# Revit family: IS_CerathermNavigo_A7295_BIM_NL
name_source: partatom
category: Plumbing Fixtures
units: mm (PartAtom-declared; Revit-internal decimal feet)

## family parameters
Always vertical = No
Cut with Voids When Loaded = No
OmniClass Number = 23.45.55.17
OmniClass Title = Mixing Faucets
Part Type = Normal
Room Calculation Point = No
Round Connector Dimension = Use Diameter
Shared = No
Work Plane-Based = No

## types (4) — shared parameters
Accesoires = https://www.idealstandard.nl
Accessories = https://www.idealstandard.nl
Afmetingen = 157 x 44 x 157 mm
AfstandsEenheid = Millimeter
AreaUnits = millimeter
Artikelreferentie = Ceratherm Navigo Thermal Shower 1-Control
AssetType = Shower Mixer
Auteur = Ideal Standard
BIMObjectName = IS_IdealStandard_ShowerMixers_CerathermNavigo_A7295
BIMobject category = Taps & Mixers
BIMobject category code = sanitary-taps-mixers
BIMobject main category = Sanitary
BIMobject main category code = sanitary
Beschrijvinggarantie = Herstellergarantie
BimObjectNaam = IS_IdealStandard_ShowerMixers_CerathermNavigo_A7295
Brand = Ideal Standard
Brand url = https://www.idealstandard.nl
Breedte = 157.100021
ConnectionType = Plumbing
CurrencyUnit = €
CurrentRevision = 1
Date of publishing = 01/04/2022
Diepte = 44 mm
Douchebak = No
DurationUnit = years
DuurEenheid = Bar
Edition number = 1
FaucetFunction = Single lever
FaucetOperation = Single lever thermal shower
FaucetType = Thermal Shower
Functiekraanwerk = Duschmischer mit 1 Bedienelementen
Garantieonderdelen = 5
Garantieunits = Jahre
GemaaktOp = 01/04/2022
Help = https://www.idealstandard.nl
Hoogte = 157.008979797363
Hulp = https://www.idealstandard.nl
IFC Classification = Sanitary Terminal
IfcExportAs = IfcValveType
IfcExportType = FAUCET
Installatieinstructies = https://www.idealstandard.nl
Installation instructions = https://www.idealstandard.nl
InstallationInstructions = https://www.idealstandard.nl
Klepmechanisme = Drehknöpfe
Lengte = 44 mm
LinearUnits = millimeter
MaintenanceInformation = https://www.idealstandard.nl
Manufacturer = Ideal Standard
Manufacturer name = Ideal Standard
ManufacturerURL = https://www.idealstandard.nl
Materiaal = Messing
Material = Verchromtes Messing
Material main = Messing
Merk = Ideal Standard
ModelReference = Ceratherm Navigo Thermal Shower 1-Control
NBS Reference Code = 45-35-70/335
NBS Reference Description = Shower mixers
Name = ShowerMixers_CerathermNavigo_A7295_IdealStandard
NettWeight = 1,85 KG
NominalDepth = 44 mm
NominalHeight = 157 mm
NominalLength = 44 mm
NominalWidth = 157 mm
Normen = ShowerMixers_CerathermNavigo_A7295_IdealStandard
OmniClass Code = 23-31- 11 00
OmniClass Description = Faucets
OppervlakteEenheid = Millimeter
PredefinedType = Shower Mixer
Product Guid = e3ce106b-39a5-4bc2-868c-9a611b3a6c7f
Product SKU = A7295
Product certification = https://www.idealstandard.nl
Product data url = https://bimobject.com
Product family = Navigo
Product group = Taps & Mixers
Product name = Ceratherm Navigo Thermal Shower 1 and Round Escutcheon
Product url = https://www.idealstandard.nl
ProductInformation = https://www.idealstandard.nl
ProductSoort = Duschmischer
Productinformatie = https://www.idealstandard.nl
QR code = http://bimobject.com
Revisie = 1
Shape = Cylindrical
Size = 157 x 44 x 157 mm
Space = Internal
SpareParts = https://www.idealstandard.nl
Technical description = https://www.idealstandard.nl
Telefoonnummer = (0228) 521-580
Testdruk = 10 bar
Toepassing = Duschmischer
Typeconnectie = Installation
Typekraanwerk = 2 Bedienknöpfe Duschmischer
UNSPSC Code = 301815
URL = https://www.idealstandard.nl
Uniclass 1.4 Code = L725111
Uniclass 1.4 Description = Taps Mixers
Uniclass 2.0 Code = PR-35-06-82
Uniclass 2.0 Description = Shower  Mixer
Uniclass 2015 Code = Pr_40_20_87_78
Uniclass 2015 Name = Shower manual water supply sets
Uniclass2015Beschrijving = Shower manual water supply sets
Uniclass2015Code = Pr_40_20_87_78
Uniclass2015Referentie = Pr_40_20_87_78
Uniclass2015Title = Shower manual water supply sets
Uniclass2015Version = v1.25
Urlproducent = https://www.idealstandard.nl
ValutaEenheid = €
Versie = 1
Version = 1
VolumeUnits = liters
Volumeunits = Liter
Vorm = Zylinder
WRASURL = https://www.wrasapprovals.co.uk
WarrantyDescription = manufacturer warranty
WarrantyDurationParts = 5
WarrantyDurationUnit = years
Wisselstukken = https://www.idealstandard.nl
Youtube clip = https://www.youtube.com
zero-valued in all types: BrutoGewicht, Nettogewicht, Vervangingskosten

## per-type parameters (varying)
| type | Afwerking | Artikelnummer | Artikelomschrijving | BarCode | Color | Description | Eigenschappen | FaucetTopDescription | Features | Finish | GTIN code | Kleur | MainColor | Model | ModelNumber | ShowerType |
| A7295AA - Ceratherm Navigo Thermal Shower 1-Control (1 Outlet)Round Escutcheon -Chrome | Chrom | A7295AA | Ceratherm Navigo Brausethermostat 1-Regler (1 Ausgang)Round Rosette -Chrom | 4015413349611 | Chrom | Ceratherm Navigo Brausethermostat 1-Regler (1 Ausgang)Round Rosette -Chrom | Brausethermostat 1-Regler (1 Ausgang)Round Rosette -Chrom | Thermal Shower 1-Control (1 Outlet)Round Escutcheon | Thermal Shower 1-Control (1 Outlet)Round Escutcheon | Chrom | https://4015413349611 | Chrom | Chrome | A7295AA | A7295AA | Thermal Shower 1-Control (1 Outlet)Round Escutcheon |
| A7295A2 - Ceratherm Navigo Thermal Shower 1-Control (2 Outlet)Round Escutcheon -Brush Gold | Pinsel Gold | A7295A2 | Ceratherm Navigo Brausethermostat 1-Regler (2 Ausgänge)Round Rosette-Brush Gold | 4015413349512 | Pinsel Gold | Ceratherm Navigo Brausethermostat 1-Regler (2 Ausgänge)Round Rosette-Brush Gold | Brausethermostat 1-Regler (2 Ausgänge)Round Rosette-Brush Gold | Thermal Shower 1-Control (2 Outlet)Round Escutcheon | Thermal Shower 1-Control (2 Outlet)Round Escutcheon | Pinsel Gold | https://4015413349512 | Pinsel Gold | Brush Gold | A7295A2 | A7295A2 | Thermal Shower 1-Control (2 Outlet)Round Escutcheon |
| A7295A5 - Ceratherm Navigo Thermal Shower 1-Control (1 Outlet)Round Escutcheon -Magnetic Grey | Magnetisches Grau | A7295A5 | Ceratherm Navigo Thermobrausebatterie 1-Steuerung (1 Ausgang) Runde Rosette – magnetisch grau | 4015413349550 | Magnetisches Grau | Ceratherm Navigo Thermobrausebatterie 1-Steuerung (1 Ausgang) Runde Rosette – magnetisch grau | Thermobrausebatterie 1-Steuerung (1 Ausgang) Runde Rosette – magnetisch grau | Thermal Shower 1-Control (1 Outlet)Round Escutcheon | Thermal Shower 1-Control (1 Outlet)Round Escutcheon | Magnetisches Grau | https://4015413349550 | Magnetisches Grau | Magnetic Grey | A7295A5 | A7295A5 | Thermal Shower 1-Control (1 Outlet)Round Escutcheon |
| A7295GN - Ceratherm Navigo Thermal Shower 1-Control (1 Outlet)Round Escutcheon -Silver Storm | Silberner Sturm | A7295GN | Ceratherm Navigo Brausethermostat 1-Regler (1 Ausgang)Round Rosette -Silver Storm | 3800828026063 | Silberner Sturm | Ceratherm Navigo Brausethermostat 1-Regler (1 Ausgang)Round Rosette -Silver Storm | Brausethermostat 1-Regler (1 Ausgang)Round Rosette -Silver Storm | Thermal Shower 1-Control (1 Outlet)Round Escutcheon | Thermal Shower 1-Control (1 Outlet)Round Escutcheon | Silberner Sturm | https://3800828026063 | Silberner Sturm | Silver Storm | A7295GN | A7295GN | Thermal Shower 1-Control (1 Outlet)Round Escutcheon |

## geometry (parser evidence)
native form markers: Sweep x4
no freeform markers — native parametric forms only
